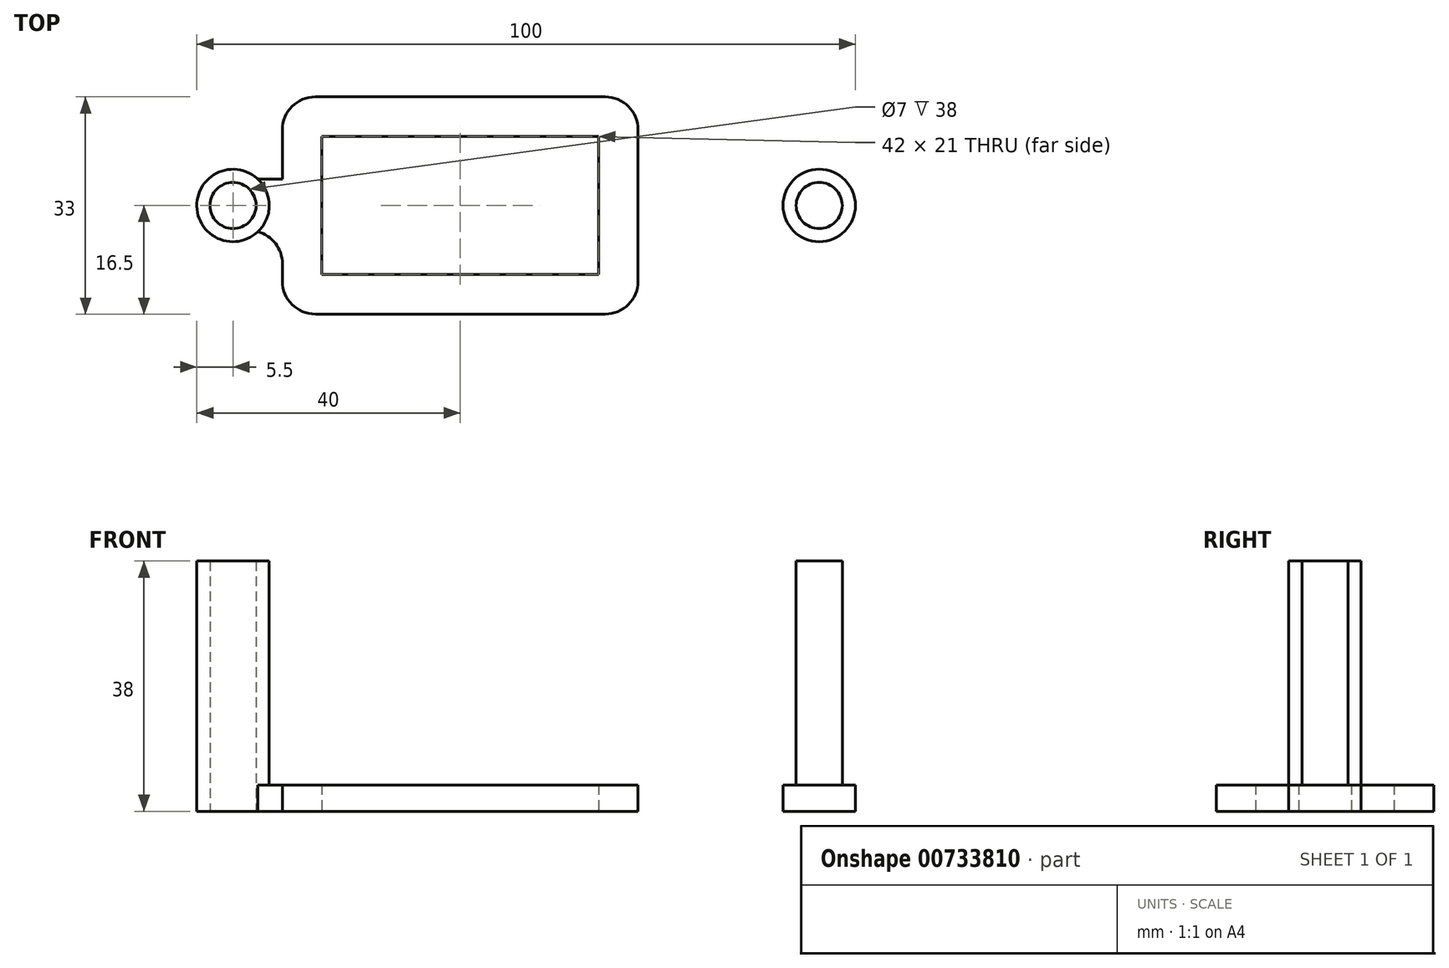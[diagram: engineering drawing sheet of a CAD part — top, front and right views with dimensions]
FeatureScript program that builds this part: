
annotation { "Feature Type Name" : "Feature", "Feature Type Description" : "" }
export const myFeature = defineFeature(function(context is Context, id is Id, definition is map)
    precondition{}
    {
        {
            var Q0;
            Q0=qCreatedBy(makeId("Top.planeOp"),FACE);
            var sketch = newSketch(context, id + "F0", { "sketchPlane" : qUnion([Q0])});
            skCircle(sketch, "E0", {"center": v(-44.5, 0) * mm, "radius": 3.5 * mm});
            skCircle(sketch, "E1", {"center": v(-44.5, 0) * mm, "radius": 5.5 * mm});
            skCircle(sketch, "E2.MirrorC", {"center": v(44.5, 0) * mm, "radius": 5.5 * mm});
            skCircle(sketch, "E3.MirrorC", {"center": v(44.5, 0) * mm, "radius": 3.5 * mm});
            skLineSegment(sketch, "E4", {"start": v(-40.73, 4) * mm, "end": v(40.73, 4) * mm});
            skLineSegment(sketch, "E5.MirrorCS", {"start": v(-40.73, -4) * mm, "end": v(40.73, -4) * mm});
            skLineSegment(sketch, "E6.bottom", {"start": v(-31, 10.5) * mm, "end": v(11, 10.5) * mm});
            skLineSegment(sketch, "E6.top", {"start": v(-31, -10.5) * mm, "end": v(11, -10.5) * mm});
            skLineSegment(sketch, "E6.left", {"start": v(-31, 10.5) * mm, "end": v(-31, -10.5) * mm});
            skLineSegment(sketch, "E6.right", {"start": v(11, 10.5) * mm, "end": v(11, -10.5) * mm});
            skPoint(sketch, "E6.middle", {"position": v(-10, 0) * mm});
            skLineSegment(sketch, "E7.0", {"start": v(-37, 16.5) * mm, "end": v(17, 16.5) * mm});
            skLineSegment(sketch, "E7.1", {"start": v(-37, 16.5) * mm, "end": v(-37, -16.5) * mm});
            skLineSegment(sketch, "E7.2", {"start": v(-37, -16.5) * mm, "end": v(17, -16.5) * mm});
            skLineSegment(sketch, "E7.3", {"start": v(17, 16.5) * mm, "end": v(17, -16.5) * mm});
            skSolve(sketch);
        }
        {
            var Q0;
            {var subQ0=sQuery(id+"F0.wireOp",EDGE,"E4");var subQ1=sQuery(id+"F0.wireOp",EDGE,"E1");var subQ2=makeQuery(id+"F0.imprint","INTERSECT",VERTEX,{"derivedFrom":[subQ1,subQ0]});Q0=makeQuery(id+"F0.imprint","IMPRINT",FACE,{"disambiguationData":[TD([[makeQuery(id+"F0.imprint","IMPRINT",EDGE,{"disambiguationData":[TD([[subQ2,1.0]])],"derivedFrom":subQ1}),-1.0]])]});}
            var Q1;
            {var subQ0=sQuery(id+"F0.wireOp",EDGE,"E4");var subQ1=sQuery(id+"F0.wireOp",EDGE,"E2.MirrorC");var subQ2=makeQuery(id+"F0.imprint","INTERSECT",VERTEX,{"derivedFrom":[subQ1,subQ0]});Q1=makeQuery(id+"F0.imprint","IMPRINT",FACE,{"disambiguationData":[TD([[makeQuery(id+"F0.imprint","IMPRINT",EDGE,{"disambiguationData":[TD([[subQ2,1.0]])],"derivedFrom":subQ1}),1.0]])]});}
            extrude(context, id + "F1", {"entities" : qUnion([Q0, Q1]), "depth" : 4 * mm, "offsetDistance" : 25 * mm});
        }
        {
            var Q0;
            Q0=makeQuery(id+"F0.imprint","IMPRINT",FACE,{"disambiguationData":[TD([[makeQuery(id+"F0.imprint","IMPRINT",EDGE,{"derivedFrom":sQuery(id+"F0.wireOp",EDGE,"E0")}),-1.0]])]});
            var Q1;
            Q1=makeQuery(id+"F0.imprint","IMPRINT",FACE,{"disambiguationData":[TD([[makeQuery(id+"F0.imprint","IMPRINT",EDGE,{"derivedFrom":sQuery(id+"F0.wireOp",EDGE,"E3.MirrorC")}),1.0]])]});
            extrude(context, id + "F2", {"entities" : qUnion([Q0, Q1]), "operationType" : NewBodyOperationType.ADD, "depth" : 38 * mm, "offsetDistance" : 25 * mm});
        }
        {
            var Q0;
            {var subQ1=sQuery(id+"F0.wireOp",EDGE,"E6.top");Q0=makeQuery(id+"F0.imprint","IMPRINT",FACE,{"disambiguationData":[TD([[makeQuery(id+"F0.imprint","IMPRINT",EDGE,{"derivedFrom":subQ1}),-1.0]])]});}
            var Q1;
            {var subQ1=sQuery(id+"F0.wireOp",EDGE,"E6.bottom");Q1=makeQuery(id+"F0.imprint","IMPRINT",FACE,{"disambiguationData":[TD([[makeQuery(id+"F0.imprint","IMPRINT",EDGE,{"derivedFrom":subQ1}),1.0]])]});}
            var Q2;
            {var subQ0=sQuery(id+"F0.wireOp",EDGE,"E7.1");var subQ1=sQuery(id+"F0.wireOp",EDGE,"E4");var subQ2=makeQuery(id+"F0.imprint","INTERSECT",VERTEX,{"derivedFrom":[subQ1,subQ0]});Q2=makeQuery(id+"F0.imprint","IMPRINT",FACE,{"disambiguationData":[TD([[makeQuery(id+"F0.imprint","IMPRINT",EDGE,{"disambiguationData":[TD([[subQ2,-1.0]])],"derivedFrom":subQ1}),-1.0]])]});}
            var Q3;
            {var subQ0=sQuery(id+"F0.wireOp",EDGE,"E7.3");var subQ1=sQuery(id+"F0.wireOp",EDGE,"E4");var subQ2=makeQuery(id+"F0.imprint","INTERSECT",VERTEX,{"derivedFrom":[subQ1,subQ0]});Q3=makeQuery(id+"F0.imprint","IMPRINT",FACE,{"disambiguationData":[TD([[makeQuery(id+"F0.imprint","IMPRINT",EDGE,{"disambiguationData":[TD([[subQ2,1.0]])],"derivedFrom":subQ1}),-1.0]])]});}
            extrude(context, id + "F3", {"entities" : qUnion([Q0, Q1, Q2, Q3]), "operationType" : NewBodyOperationType.ADD, "depth" : 4 * mm, "offsetDistance" : 25 * mm});
        }
        {
            var Q0;
            Q0=makeQuery(id+"F1.opExtrude","SWEPT_EDGE",EDGE,{"disambiguationData":[OSD([sQuery(id+"F0.wireOp",EDGE,"E1"),sQuery(id+"F0.wireOp",EDGE,"E4")])]});
            var Q1;
            Q1=makeQuery(id+"F1.opExtrude","SWEPT_EDGE",EDGE,{"disambiguationData":[OSD([sQuery(id+"F0.wireOp",EDGE,"E4"),sQuery(id+"F0.wireOp",EDGE,"E7.1")])]});
            var Q2;
            Q2=makeQuery(id+"F1.opExtrude","SWEPT_EDGE",EDGE,{"disambiguationData":[OSD([sQuery(id+"F0.wireOp",EDGE,"E5.MirrorCS"),sQuery(id+"F0.wireOp",EDGE,"E7.1")])]});
            var Q3;
            Q3=makeQuery(id+"F1.opExtrude","SWEPT_EDGE",EDGE,{"disambiguationData":[OSD([sQuery(id+"F0.wireOp",EDGE,"E1"),sQuery(id+"F0.wireOp",EDGE,"E5.MirrorCS")])]});
            var Q4;
            Q4=makeQuery(id+"F1.opExtrude","SWEPT_EDGE",EDGE,{"disambiguationData":[OSD([sQuery(id+"F0.wireOp",EDGE,"E4"),sQuery(id+"F0.wireOp",EDGE,"E7.3")])]});
            var Q5;
            Q5=makeQuery(id+"F1.opExtrude","SWEPT_EDGE",EDGE,{"disambiguationData":[OSD([sQuery(id+"F0.wireOp",EDGE,"E5.MirrorCS"),sQuery(id+"F0.wireOp",EDGE,"E7.3")])]});
            var Q6;
            Q6=makeQuery(id+"F1.opExtrude","SWEPT_EDGE",EDGE,{"disambiguationData":[OSD([sQuery(id+"F0.wireOp",EDGE,"E2.MirrorC"),sQuery(id+"F0.wireOp",EDGE,"E5.MirrorCS")])]});
            var Q7;
            Q7=makeQuery(id+"F1.opExtrude","SWEPT_EDGE",EDGE,{"disambiguationData":[OSD([sQuery(id+"F0.wireOp",EDGE,"E2.MirrorC"),sQuery(id+"F0.wireOp",EDGE,"E4")])]});
            var Q8;
            Q8=makeQuery(id+"F3.opExtrude","SWEPT_EDGE",EDGE,{"disambiguationData":[OSD([sQuery(id+"F0.wireOp",EDGE,"E7.0"),sQuery(id+"F0.wireOp",EDGE,"E7.3")])]});
            var Q9;
            Q9=makeQuery(id+"F3.opExtrude","SWEPT_EDGE",EDGE,{"disambiguationData":[OSD([sQuery(id+"F0.wireOp",EDGE,"E7.0"),sQuery(id+"F0.wireOp",EDGE,"E7.1")])]});
            var Q10;
            Q10=makeQuery(id+"F3.opExtrude","SWEPT_EDGE",EDGE,{"disambiguationData":[OSD([sQuery(id+"F0.wireOp",EDGE,"E7.1"),sQuery(id+"F0.wireOp",EDGE,"E7.2")])]});
            var Q11;
            Q11=makeQuery(id+"F3.opExtrude","SWEPT_EDGE",EDGE,{"disambiguationData":[OSD([sQuery(id+"F0.wireOp",EDGE,"E7.2"),sQuery(id+"F0.wireOp",EDGE,"E7.3")])]});
            fillet(context, id + "F4", {"entities" : qUnion([Q0, Q1, Q2, Q3, Q4, Q5, Q6, Q7, Q8, Q9, Q10, Q11]), "radius" : 5 * mm, "tangentPropagation" : true, "allowEdgeOverflow" : false});
        }
    });
